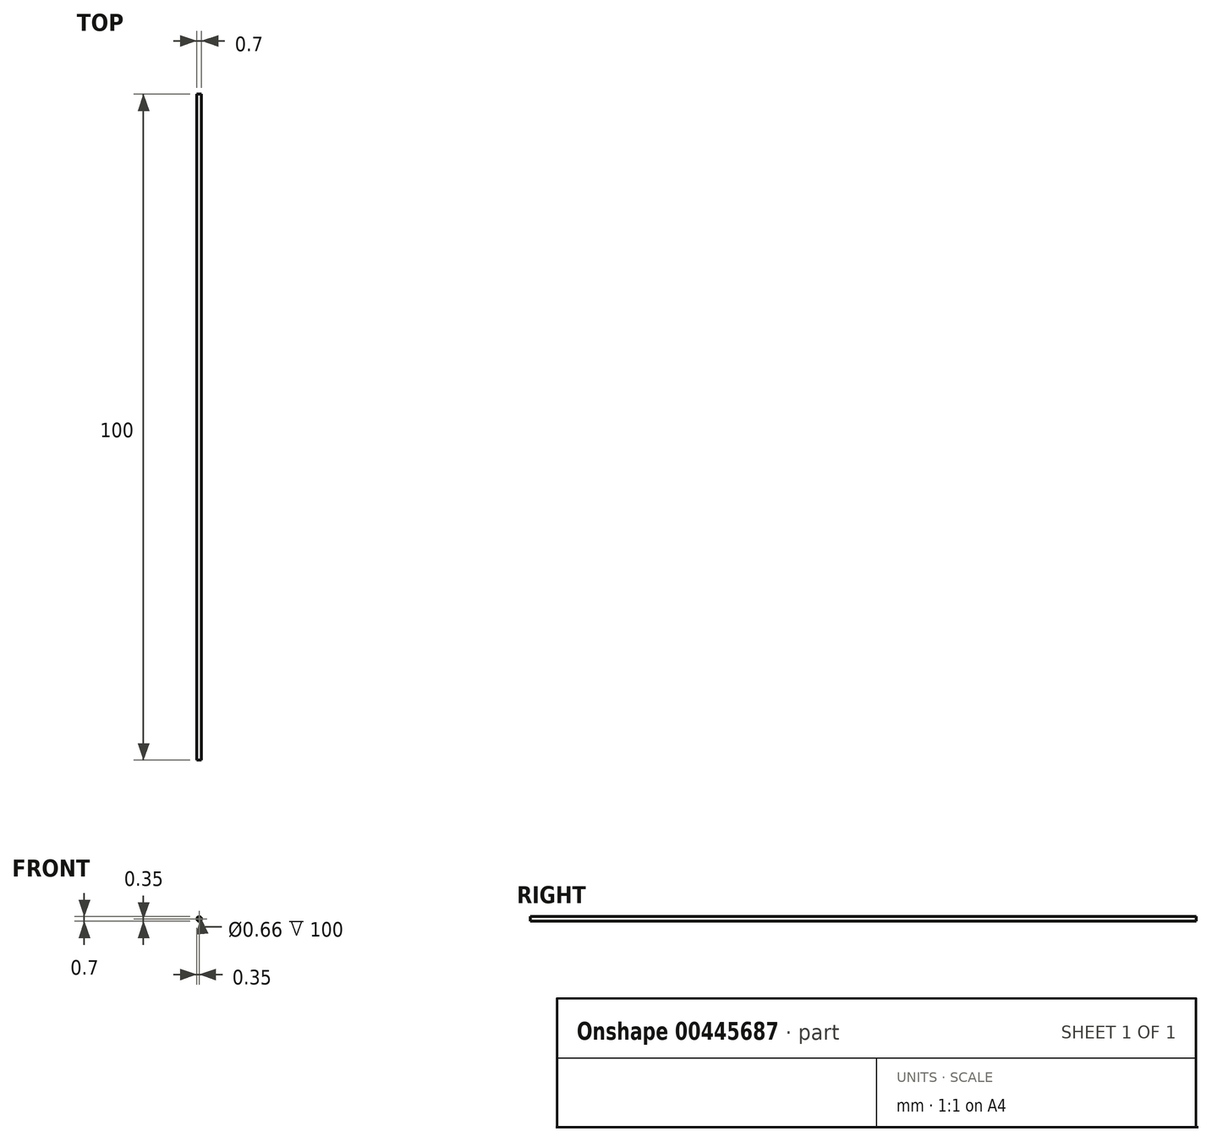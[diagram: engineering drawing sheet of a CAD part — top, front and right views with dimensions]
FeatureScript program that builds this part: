
annotation { "Feature Type Name" : "Feature", "Feature Type Description" : "" }
export const myFeature = defineFeature(function(context is Context, id is Id, definition is map)
    precondition{}
    {
        {
            var Q0;
            Q0=qCreatedBy(makeId("Front.planeOp"),FACE);
            var sketch = newSketch(context, id + "F0", { "sketchPlane" : qUnion([Q0])});
            skCircle(sketch, "E0", {"center": v(0, 0) * mm, "radius": 0.35 * mm});
            skSolve(sketch);
        }
        {
            var Q0;
            Q0 = qSketchRegion(id + "F0", true);
            extrude(context, id + "F1", {"entities" : qUnion([Q0]), "depth" : 100 * mm});
        }
        {
            var Q0;
            Q0=sQuery(id+"F0.wireOp",VERTEX,"E0.center");
            var Q1;
            Q1=makeQuery(id+"F1.opExtrude","SWEPT_BODY",BODY,{"disambiguationData":[OSD([sQuery(id+"F0.wireOp",EDGE,"E0")])]});
            hole(context, id + "F2", {"style" : HoleStyle.SIMPLE, "endStyle" : HoleEndStyle.BLIND, "oppositeDirection" : true, "holeDiameter" : 0.66 * mm, "holeDepth" : 100 * mm, "isTappedThrough" : true, "tappedDepth" : 12.7 * mm, "tapClearance" : 3, "locations" : qUnion([Q0]), "scope" : qUnion([Q1])});
        }
    });
